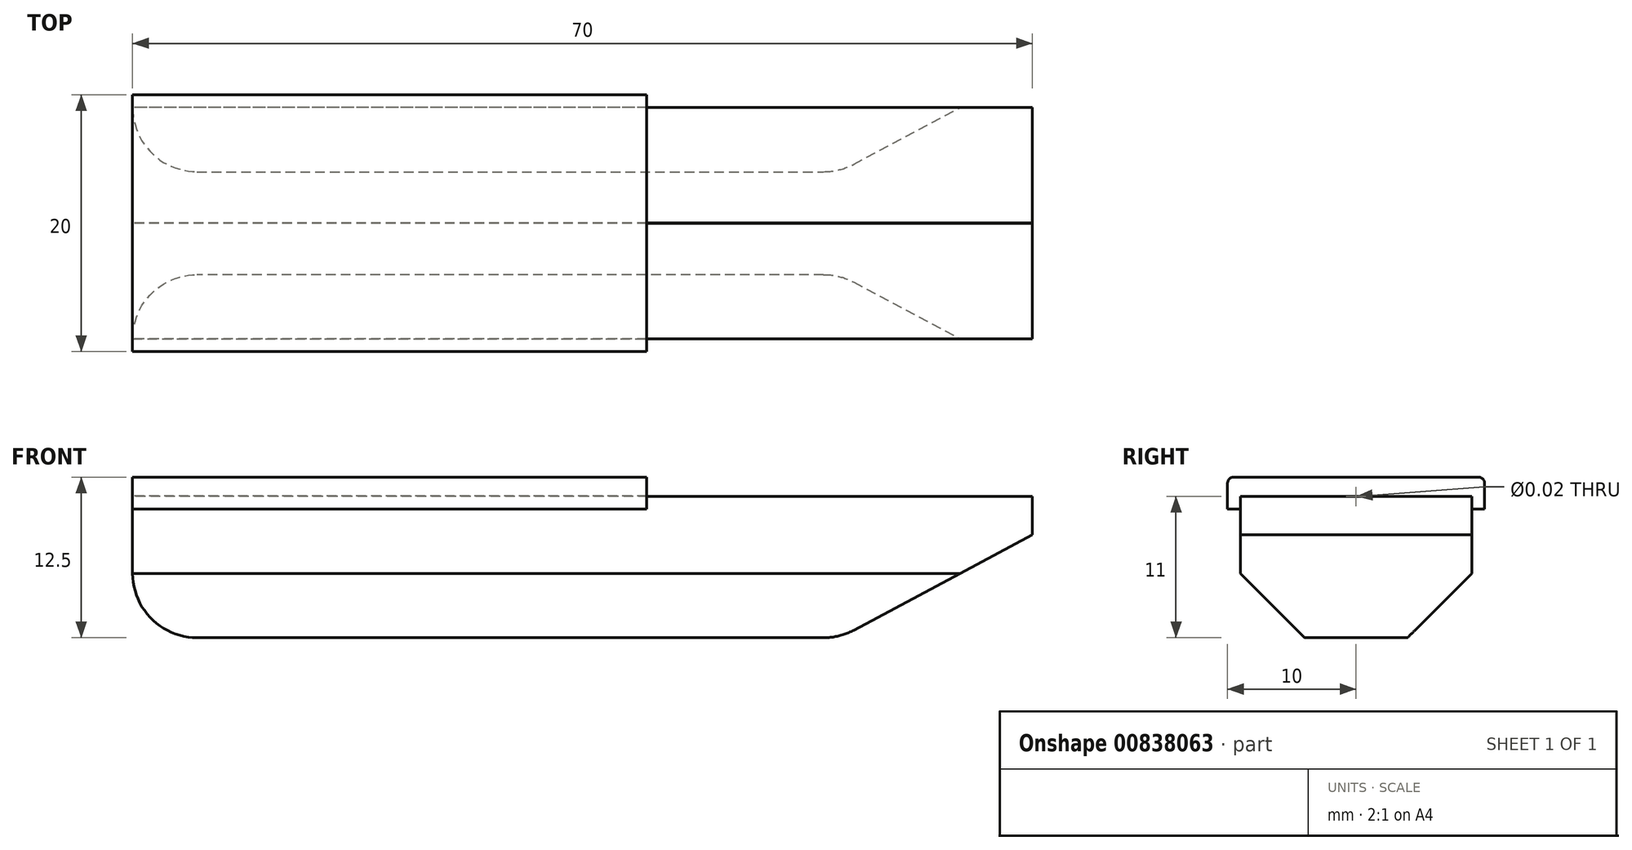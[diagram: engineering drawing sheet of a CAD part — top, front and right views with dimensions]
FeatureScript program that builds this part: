
annotation { "Feature Type Name" : "Feature", "Feature Type Description" : "" }
export const myFeature = defineFeature(function(context is Context, id is Id, definition is map)
    precondition{}
    {
        {
            var Q0;
            Q0=qCreatedBy(makeId("Right.planeOp"),FACE);
            var sketch = newSketch(context, id + "F0", { "sketchPlane" : qUnion([Q0])});
            skLineSegment(sketch, "E0.bottom", {"start": v(0, 0) * mm, "end": v(-9, 0) * mm});
            skLineSegment(sketch, "E0.top", {"start": v(0, -11) * mm, "end": v(-9, -11) * mm});
            skLineSegment(sketch, "E0.left", {"start": v(0, 0) * mm, "end": v(0, -11) * mm});
            skLineSegment(sketch, "E0.right", {"start": v(-9, 0) * mm, "end": v(-9, -11) * mm});
            skLineSegment(sketch, "E1.bottom", {"start": v(0, 0) * mm, "end": v(9, 0) * mm});
            skLineSegment(sketch, "E1.top", {"start": v(0, -11) * mm, "end": v(9, -11) * mm});
            skLineSegment(sketch, "E1.right", {"start": v(9, 0) * mm, "end": v(9, -11) * mm});
            skSolve(sketch);
        }
        {
            var Q0;
            Q0=qCreatedBy(makeId("Right.planeOp"),FACE);
            var sketch = newSketch(context, id + "F1", { "sketchPlane" : qUnion([Q0])});
            skLineSegment(sketch, "E2.bottom", {"start": v(0, 0) * mm, "end": v(-10, 0) * mm});
            skLineSegment(sketch, "E2.top", {"start": v(0, -1) * mm, "end": v(-10, -1) * mm});
            skLineSegment(sketch, "E2.left", {"start": v(0, 0) * mm, "end": v(0, -1) * mm});
            skLineSegment(sketch, "E2.right", {"start": v(-10, 0) * mm, "end": v(-10, -1) * mm});
            skLineSegment(sketch, "E3.bottom", {"start": v(0, 0) * mm, "end": v(10, 0) * mm});
            skLineSegment(sketch, "E3.top", {"start": v(0, -1) * mm, "end": v(10, -1) * mm});
            skLineSegment(sketch, "E3.right", {"start": v(10, 0) * mm, "end": v(10, -1) * mm});
            skLineSegment(sketch, "E4.top", {"start": v(0, 1.5) * mm, "end": v(-10, 1.5) * mm});
            skLineSegment(sketch, "E4.left", {"start": v(0, 0) * mm, "end": v(0, 1.5) * mm});
            skLineSegment(sketch, "E4.right", {"start": v(-10, 0) * mm, "end": v(-10, 1.5) * mm});
            skLineSegment(sketch, "E5.bottom", {"start": v(0, 1.5) * mm, "end": v(10, 1.5) * mm});
            skLineSegment(sketch, "E5.left", {"start": v(0, 1.5) * mm, "end": v(0, 0) * mm});
            skLineSegment(sketch, "E5.right", {"start": v(10, 1.5) * mm, "end": v(10, 0) * mm});
            skSolve(sketch);
        }
        {
            var Q0;
            Q0 = qSketchRegion(id + "F0", true);
            extrude(context, id + "F2", {"entities" : qUnion([Q0]), "depth" : 70 * mm, "offsetDistance" : 25 * mm});
        }
        {
            var Q0;
            Q0 = qSketchRegion(id + "F1", true);
            extrude(context, id + "F3", {"entities" : qUnion([Q0]), "operationType" : NewBodyOperationType.ADD, "depth" : 40 * mm, "offsetDistance" : 25 * mm});
        }
        {
            var Q0;
            Q0=sQuery(id+"F0.wireOp",VERTEX,"E0.bottom.start");
            var Q1;
            Q1=makeQuery(id+"F2.opExtrude","SWEPT_BODY",BODY,{"disambiguationData":[OSD([sQuery(id+"F0.wireOp",EDGE,"E0.bottom"),sQuery(id+"F0.wireOp",EDGE,"E0.top"),sQuery(id+"F0.wireOp",EDGE,"E0.right"),sQuery(id+"F0.wireOp",EDGE,"E1.bottom"),sQuery(id+"F0.wireOp",EDGE,"E1.top"),sQuery(id+"F0.wireOp",EDGE,"E1.right")])]});
            hole(context, id + "F4", {"style" : HoleStyle.SIMPLE, "endStyle" : HoleEndStyle.THROUGH, "oppositeDirection" : true, "standardTappedOrClearance" : lookupTablePath({ "standard" : "ANSI", "size" : "9/16 (0.56)", "type" : "Drilled" }), "standardBlindInLast" : lookupTablePath({ "standard" : "ANSI", "size" : "9/16", "type" : "Drilled" }), "holeDiameter" : 9 / 406.4 * mm, "majorDiameter" : 5 * mm, "isTappedThrough" : true, "tappedDepth" : 12 * mm, "tapClearance" : 3, "startFromSketch" : true, "locations" : qUnion([Q0]), "scope" : qUnion([Q1])});
        }
        {
            var Q0;
            Q0=makeQuery(id+"F2.opExtrude","CAP_EDGE",EDGE,{"disambiguationData":[OSD([sQuery(id+"F0.wireOp",EDGE,"E0.top"),sQuery(id+"F0.wireOp",EDGE,"E1.top")])],"isStart":false});
            chamfer(context, id + "F5", {"entities" : qUnion([Q0]), "chamferType" : ChamferType.TWO_OFFSETS, "width1" : 15 * mm, "oppositeDirection" : false, "width2" : 8 * mm, "tangentPropagation" : true});
        }
        {
            var Q0;
            Q0=makeQuery(id+"F2.opExtrude","SWEPT_EDGE",EDGE,{"disambiguationData":[OSD([sQuery(id+"F0.wireOp",EDGE,"E1.top"),sQuery(id+"F0.wireOp",EDGE,"E1.right")])]});
            var Q1;
            Q1=makeQuery(id+"F2.opExtrude","SWEPT_EDGE",EDGE,{"disambiguationData":[OSD([sQuery(id+"F0.wireOp",EDGE,"E0.top"),sQuery(id+"F0.wireOp",EDGE,"E0.right")])]});
            chamfer(context, id + "F6", {"entities" : qUnion([Q0, Q1]), "width" : 5 * mm, "tangentPropagation" : true});
        }
        {
            var Q0;
            {var subQ0=sQuery(id+"F0.wireOp",EDGE,"E1.top");var subQ1=sQuery(id+"F0.wireOp",EDGE,"E0.top");Q0=makeQuery(id+"F5.opChamfer","BLEND_EDGE",EDGE,{"blendedFrom":[makeQuery(id+"F2.opExtrude","CAP_EDGE",EDGE,{"disambiguationData":[OSD([subQ1,subQ0])],"isStart":false}),makeQuery(id+"F2.opExtrude","SWEPT_FACE",FACE,{"disambiguationData":[OSD([subQ1,subQ0])]})],"blendedInto":[makeQuery(id+"F2.opExtrude","SWEPT_FACE",FACE,{"disambiguationData":[OSD([subQ1,subQ0])]})]});}
            var Q1;
            Q1=makeQuery(id+"F2.opExtrude","CAP_EDGE",EDGE,{"disambiguationData":[OSD([sQuery(id+"F0.wireOp",EDGE,"E0.top"),sQuery(id+"F0.wireOp",EDGE,"E1.top")])],"isStart":true});
            fillet(context, id + "F7", {"entities" : qUnion([Q0, Q1]), "radius" : 5 * mm, "tangentPropagation" : true, "allowEdgeOverflow" : false});
        }
        {
            var Q0;
            Q0=makeQuery(id+"F3.opExtrude","SWEPT_EDGE",EDGE,{"disambiguationData":[OSD([sQuery(id+"F1.wireOp",EDGE,"E4.top"),sQuery(id+"F1.wireOp",EDGE,"E4.right")])]});
            var Q1;
            Q1=makeQuery(id+"F4.hole-0.boolean.opBoolean","INTERSECT",EDGE,{"disambiguationData":[OD(1.0)],"derivedFrom":[makeQuery(id+"F3.opExtrude","SWEPT_FACE",FACE,{"disambiguationData":[OSD([sQuery(id+"F1.wireOp",EDGE,"E4.top"),sQuery(id+"F1.wireOp",EDGE,"E5.bottom")])]}),makeQuery(id+"F4.hole-0.opRevolve","SWEPT_FACE",FACE,{"disambiguationData":[OSD([sQuery(id+"F4.hole-0.sketch.wireOp",EDGE,"core_line_2")])]})]});
            var Q2;
            Q2=makeQuery(id+"F3.opExtrude","SWEPT_EDGE",EDGE,{"disambiguationData":[OSD([sQuery(id+"F1.wireOp",EDGE,"E5.bottom"),sQuery(id+"F1.wireOp",EDGE,"E5.right")])]});
            var Q3;
            Q3=makeQuery(id+"F4.hole-0.boolean.opBoolean","INTERSECT",EDGE,{"disambiguationData":[OD(0.0)],"derivedFrom":[makeQuery(id+"F3.opExtrude","SWEPT_FACE",FACE,{"disambiguationData":[OSD([sQuery(id+"F1.wireOp",EDGE,"E4.top"),sQuery(id+"F1.wireOp",EDGE,"E5.bottom")])]}),makeQuery(id+"F4.hole-0.opRevolve","SWEPT_FACE",FACE,{"disambiguationData":[OSD([sQuery(id+"F4.hole-0.sketch.wireOp",EDGE,"core_line_2")])]})]});
            fillet(context, id + "F8", {"entities" : qUnion([Q0, Q1, Q2, Q3]), "radius" : .5 * mm, "tangentPropagation" : true, "allowEdgeOverflow" : false});
        }
    });
